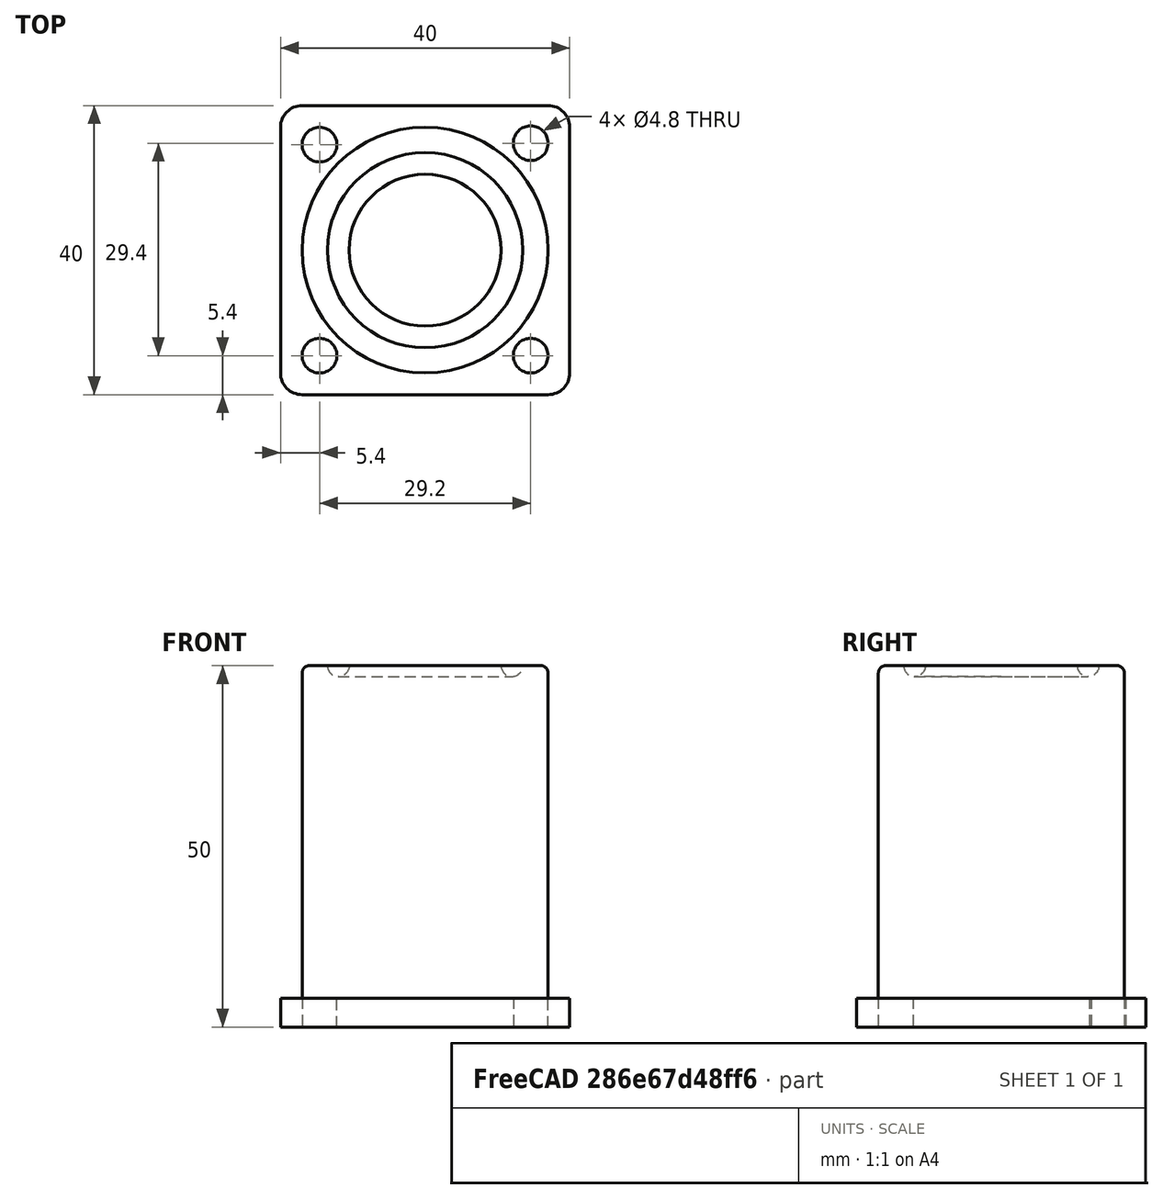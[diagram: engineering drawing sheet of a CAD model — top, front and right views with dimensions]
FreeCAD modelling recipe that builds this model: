
FCSTD DOCUMENT  (FreeCAD 0.21R33694 (Git))
Label: OJT1_T15R03.pota_tula
License: All rights reserved
LicenseURL: http://en.wikipedia.org/wiki/All_rights_reserved
objects: Part::Cylinder×5, Part::Fuse×3, Part::Cut×3, Part::Fillet×2, Part::Box×1, Part::Torus×1
note: 15 computed .brp shape members not serialized (recipe doc carries the construction recipe); baked Part::Feature solids carry a one-line shape summary decoded from their .brp

FEATURE [Part::Box] Box  label="Cub"
  AttacherType = Attacher::AttachEngine3D
  Height = 4
  Length = 40
  Width = 40
FEATURE [Part::Cylinder] Cylinder  label="Cilindre"
  Angle = 360
  AttacherType = Attacher::AttachEngine3D
  FirstAngle = 0
  Height = 10
  Placement = pos=(34.6,34.8,0) rot=(0,0,1;0rad)
  Radius = 2.4
  SecondAngle = 0
FEATURE [Part::Cylinder] Cylinder001  label="Cilindre001"
  Angle = 360
  AttacherType = Attacher::AttachEngine3D
  FirstAngle = 0
  Height = 10
  Placement = pos=(5.4,34.6,0) rot=(0,0,1;0rad)
  Radius = 2.4
  SecondAngle = 0
FEATURE [Part::Cylinder] Cylinder002  label="Cilindre002"
  Angle = 360
  AttacherType = Attacher::AttachEngine3D
  FirstAngle = 0
  Height = 10
  Placement = pos=(5.4,5.4,0) rot=(0,0,1;0rad)
  Radius = 2.4
  SecondAngle = 0
FEATURE [Part::Cylinder] Cylinder003  label="Cilindre003"
  Angle = 360
  AttacherType = Attacher::AttachEngine3D
  FirstAngle = 0
  Height = 10
  Placement = pos=(34.6,5.4,0) rot=(0,0,1;0rad)
  Radius = 2.4
  SecondAngle = 0
FEATURE [Part::Fuse] Fusion
  Base = -> Cylinder
  Refine = true
  Tool = -> Cylinder001
FEATURE [Part::Fuse] Fusion001
  Base = -> Cylinder003
  Refine = true
  Tool = -> Fusion
FEATURE [Part::Cut] Cut
  Base = -> Box
  Refine = true
  Tool = -> Fusion001
FEATURE [Part::Cut] Cut001
  Base = -> Cut
  Refine = true
  Tool = -> Cylinder002
FEATURE [Part::Fillet] Fillet
  Base = -> Cut001
  Edges = 4 edges r=3: [Edge1,Edge3,Edge6,Edge15]
FEATURE [Part::Cylinder] Cylinder004  label="Cilindre004"
  Angle = 360
  AttacherType = Attacher::AttachEngine3D
  FirstAngle = 0
  Height = 50
  Placement = pos=(20,20,0) rot=(0,0,1;0rad)
  Radius = 17
  SecondAngle = 0
FEATURE [Part::Fillet] Fillet001
  Base = -> Cylinder004
  Edges = 1 edges r=1: [Edge3]
FEATURE [Part::Fuse] Fusion002
  Base = -> Fillet
  Refine = true
  Tool = -> Fillet001
FEATURE [Part::Torus] Torus
  Angle1 = -180
  Angle2 = 180
  Angle3 = 360
  AttacherType = Attacher::AttachEngine3D
  Placement = pos=(20,20,50) rot=(0,0,1;0rad)
  Radius1 = 12
  Radius2 = 1.5
FEATURE [Part::Cut] Cut002
  Base = -> Fusion002
  Refine = true
  Tool = -> Torus
